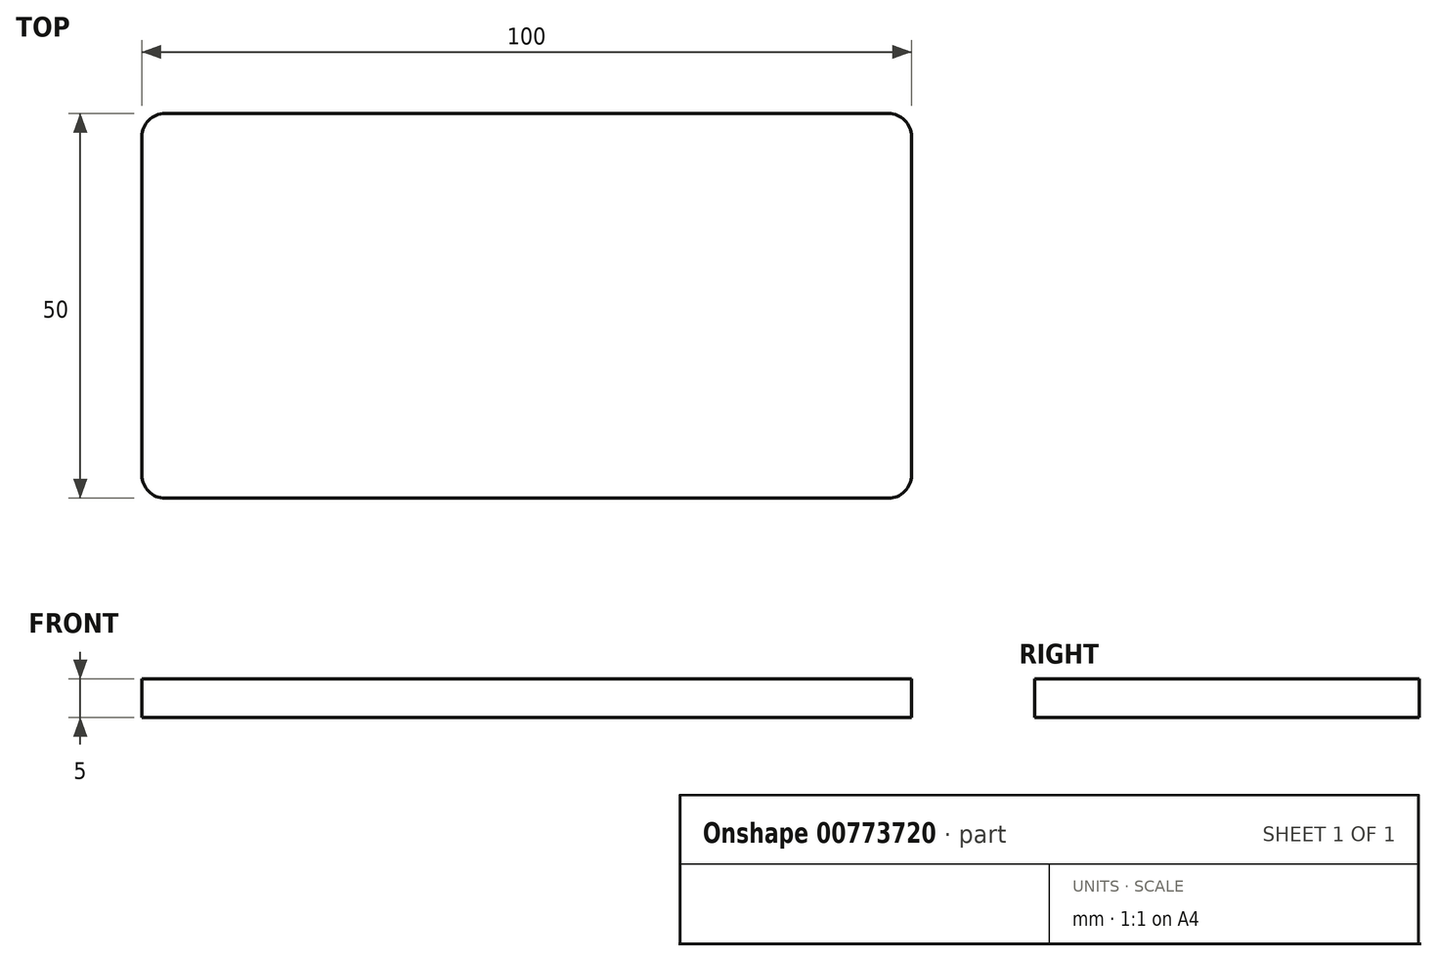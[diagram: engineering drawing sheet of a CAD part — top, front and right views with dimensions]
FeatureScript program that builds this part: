
annotation { "Feature Type Name" : "Feature", "Feature Type Description" : "" }
export const myFeature = defineFeature(function(context is Context, id is Id, definition is map)
    precondition{}
    {
        {
            var Q0;
            Q0=qCreatedBy(makeId("Top.planeOp"),FACE);
            var sketch = newSketch(context, id + "F0", { "sketchPlane" : qUnion([Q0])});
            skLineSegment(sketch, "E0.bottom", {"start": v(20.72, 31.09) * mm, "end": v(120.72, 31.09) * mm});
            skLineSegment(sketch, "E0.top", {"start": v(20.72, -18.91) * mm, "end": v(120.72, -18.91) * mm});
            skLineSegment(sketch, "E0.left", {"start": v(20.72, 31.09) * mm, "end": v(20.72, -18.91) * mm});
            skLineSegment(sketch, "E0.right", {"start": v(120.72, 31.09) * mm, "end": v(120.72, -18.91) * mm});
            skSolve(sketch);
        }
        {
            var Q0;
            Q0=makeQuery(id+"F0.imprint","IMPRINT",FACE,{"disambiguationData":[TD([[makeQuery(id+"F0.imprint","IMPRINT",EDGE,{"derivedFrom":sQuery(id+"F0.wireOp",EDGE,"E0.bottom")}),-1.0]])]});
            extrude(context, id + "F1", {"entities" : qUnion([Q0]), "depth" : 5 * mm, "offsetDistance" : 25 * mm});
        }
        {
            var Q0;
            Q0=makeQuery(id+"F1.opExtrude","SWEPT_EDGE",EDGE,{"disambiguationData":[OSD([sQuery(id+"F0.wireOp",EDGE,"E0.bottom"),sQuery(id+"F0.wireOp",EDGE,"E0.left")])]});
            var Q1;
            Q1=makeQuery(id+"F1.opExtrude","SWEPT_EDGE",EDGE,{"disambiguationData":[OSD([sQuery(id+"F0.wireOp",EDGE,"E0.bottom"),sQuery(id+"F0.wireOp",EDGE,"E0.right")])]});
            var Q2;
            Q2=makeQuery(id+"F1.opExtrude","SWEPT_EDGE",EDGE,{"disambiguationData":[OSD([sQuery(id+"F0.wireOp",EDGE,"E0.top"),sQuery(id+"F0.wireOp",EDGE,"E0.right")])]});
            var Q3;
            Q3=makeQuery(id+"F1.opExtrude","SWEPT_EDGE",EDGE,{"disambiguationData":[OSD([sQuery(id+"F0.wireOp",EDGE,"E0.top"),sQuery(id+"F0.wireOp",EDGE,"E0.left")])]});
            fillet(context, id + "F2", {"entities" : qUnion([Q0, Q1, Q2, Q3]), "radius" : 3 * mm, "tangentPropagation" : true, "allowEdgeOverflow" : false});
        }
    });
